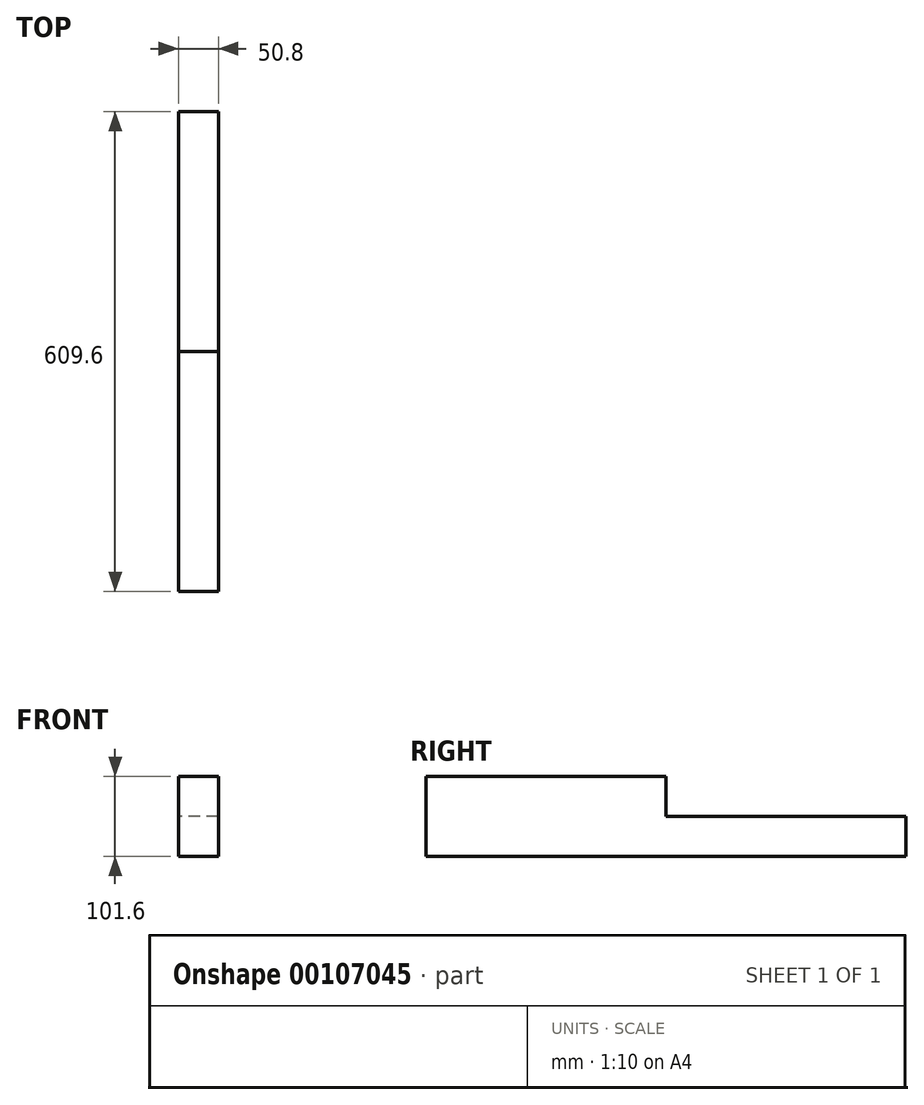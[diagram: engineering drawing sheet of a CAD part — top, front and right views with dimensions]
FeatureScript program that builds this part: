
annotation { "Feature Type Name" : "Feature", "Feature Type Description" : "" }
export const myFeature = defineFeature(function(context is Context, id is Id, definition is map)
    precondition{}
    {
        {
            var Q0;
            Q0=qCreatedBy(makeId("Right.planeOp"),FACE);
            var sketch = newSketch(context, id + "F0", { "sketchPlane" : qUnion([Q0])});
            skLineSegment(sketch, "E0.bottom", {"start": v(-120.26, 78.7) * mm, "end": v(184.54, 78.7) * mm});
            skLineSegment(sketch, "E0.top", {"start": v(-120.26, -22.9) * mm, "end": v(184.54, -22.9) * mm});
            skLineSegment(sketch, "E0.left", {"start": v(-120.26, 78.7) * mm, "end": v(-120.26, -22.9) * mm});
            skLineSegment(sketch, "E0.right", {"start": v(184.54, 78.7) * mm, "end": v(184.54, -22.9) * mm});
            skLineSegment(sketch, "E1.bottom", {"start": v(184.54, -22.9) * mm, "end": v(489.34, -22.9) * mm});
            skLineSegment(sketch, "E1.top", {"start": v(184.54, 27.9) * mm, "end": v(489.34, 27.9) * mm});
            skLineSegment(sketch, "E1.left", {"start": v(184.54, -22.9) * mm, "end": v(184.54, 27.9) * mm});
            skLineSegment(sketch, "E1.right", {"start": v(489.34, -22.9) * mm, "end": v(489.34, 27.9) * mm});
            skSolve(sketch);
        }
        {
            var Q0;
            Q0=makeQuery(id+"F0.imprint","IMPRINT",FACE,{"disambiguationData":[TD([[makeQuery(id+"F0.imprint","IMPRINT",EDGE,{"derivedFrom":sQuery(id+"F0.wireOp",EDGE,"E0.bottom")}),-1.0]])]});
            var Q1;
            Q1=makeQuery(id+"F0.imprint","IMPRINT",FACE,{"disambiguationData":[TD([[makeQuery(id+"F0.imprint","IMPRINT",EDGE,{"derivedFrom":sQuery(id+"F0.wireOp",EDGE,"E1.bottom")}),1.0]])]});
            extrude(context, id + "F1", {"entities" : qUnion([Q0, Q1]), "depth" : 50.8 * mm});
        }
    });
